annotation { "Feature Type Name" : "Feature", "Feature Type Description" : "" }
export const myFeature = defineFeature(function(context is Context, id is Id, definition is map)
    precondition{}
    {
        {
            var Q0;
            Q0=qCreatedBy(makeId("Top.planeOp"),FACE);
            var sketch = newSketch(context, id + "F0", { "sketchPlane" : qUnion([Q0])});
            skLineSegment(sketch, "E0.bottom", {"start": v(-32.9, 33.13) * mm, "end": v(31.1, 33.13) * mm});
            skLineSegment(sketch, "E0.top", {"start": v(-32.9, -20.87) * mm, "end": v(29.6, -20.87) * mm});
            skLineSegment(sketch, "E0.left", {"start": v(-32.9, 33.13) * mm, "end": v(-32.9, -20.87) * mm});
            skLineSegment(sketch, "E0.right", {"start": v(34.1, 27.13) * mm, "end": v(34.1, -5.87) * mm});
            skLineSegment(sketch, "E1", {"start": v(31.1, 33.13) * mm, "end": v(31.1, 30.13) * mm});
            skLineSegment(sketch, "E2", {"start": v(31.1, -19.37) * mm, "end": v(31.1, -8.87) * mm});
            skLineSegment(sketch, "E3", {"start": v(31.1, 30.13) * mm, "end": v(34.1, 27.13) * mm});
            skLineSegment(sketch, "E4", {"start": v(31.1, -8.87) * mm, "end": v(34.1, -5.87) * mm});
            skLineSegment(sketch, "E5", {"start": v(31.1, 30.13) * mm, "end": v(31.1, -8.87) * mm, "construction": true});
            skCircle(sketch, "E6", {"center": v(31.1, 26.13) * mm, "radius": 1.5 * mm});
            skCircle(sketch, "E7", {"center": v(31.1, -4.87) * mm, "radius": 1.5 * mm});
            skCircle(sketch, "E8", {"center": v(-17.9, -17.87) * mm, "radius": 1.5 * mm});
            skLineSegment(sketch, "E9", {"start": v(-32.9, 6.13) * mm, "end": v(34.1, 6.13) * mm, "construction": true});
            skPoint(sketch, "E9.endSnap0", {"position": v(34.1, 10.63) * mm});
            skCircle(sketch, "E10.MirrorC", {"center": v(-17.9, 30.13) * mm, "radius": 1.5 * mm});
            skLineSegment(sketch, "E11", {"start": v(31.1, -19.37) * mm, "end": v(29.6, -20.87) * mm});
            skPoint(sketch, "E12.orphan", {"position": v(31.1, -20.87) * mm});
            skSolve(sketch);
        }
        {
            var Q0;
            Q0=makeQuery(id+"F0.imprint","IMPRINT",FACE,{"disambiguationData":[TD([[makeQuery(id+"F0.imprint","IMPRINT",EDGE,{"derivedFrom":sQuery(id+"F0.wireOp",EDGE,"E0.bottom")}),-1.0]])]});
            extrude(context, id + "F1", {"entities" : qUnion([Q0]), "depth" : 1.5 * mm});
        }
        {
            var Q0;
            Q0=makeQuery(id+"F1.opExtrude","CAP_FACE",FACE,{"disambiguationData":[OSD([sQuery(id+"F0.wireOp",EDGE,"E0.bottom"),sQuery(id+"F0.wireOp",EDGE,"E0.top"),sQuery(id+"F0.wireOp",EDGE,"E0.left"),sQuery(id+"F0.wireOp",EDGE,"E0.right"),sQuery(id+"F0.wireOp",EDGE,"E1"),sQuery(id+"F0.wireOp",EDGE,"E2"),sQuery(id+"F0.wireOp",EDGE,"E3"),sQuery(id+"F0.wireOp",EDGE,"E4"),sQuery(id+"F0.wireOp",EDGE,"E6"),sQuery(id+"F0.wireOp",EDGE,"E7"),sQuery(id+"F0.wireOp",EDGE,"E8"),sQuery(id+"F0.wireOp",EDGE,"E10.MirrorC"),sQuery(id+"F0.wireOp",EDGE,"E11")])],"isStart":true});
            var sketch = newSketch(context, id + "F2", { "sketchPlane" : qUnion([Q0])});
            skLineSegment(sketch, "E13.bottom", {"start": v(14.85, -30.13) * mm, "end": v(29.85, -30.13) * mm});
            skLineSegment(sketch, "E13.top", {"start": v(14.85, -32.13) * mm, "end": v(29.85, -32.13) * mm});
            skLineSegment(sketch, "E13.left", {"start": v(14.85, -30.13) * mm, "end": v(14.85, -32.13) * mm});
            skLineSegment(sketch, "E13.right", {"start": v(29.85, -30.13) * mm, "end": v(29.85, -32.13) * mm});
            skLineSegment(sketch, "E14.bottom", {"start": v(12.85, -32.13) * mm, "end": v(-2.15, -32.13) * mm});
            skLineSegment(sketch, "E14.top", {"start": v(12.85, -30.13) * mm, "end": v(-2.15, -30.13) * mm});
            skLineSegment(sketch, "E14.left", {"start": v(12.85, -32.13) * mm, "end": v(12.85, -30.13) * mm});
            skLineSegment(sketch, "E14.right", {"start": v(-2.15, -32.13) * mm, "end": v(-2.15, -30.13) * mm});
            skCircle(sketch, "E15", {"center": v(-5.15, -28.13) * mm, "radius": 3 * mm});
            skCircle(sketch, "E16", {"center": v(-11.15, -28.13) * mm, "radius": 3 * mm});
            skSolve(sketch);
        }
        {
            var Q0;
            Q0=makeQuery(id+"F2.imprint","IMPRINT",FACE,{"disambiguationData":[TD([[makeQuery(id+"F2.imprint","IMPRINT",EDGE,{"derivedFrom":sQuery(id+"F2.wireOp",EDGE,"E14.bottom")}),-1.0]])]});
            var Q1;
            Q1=makeQuery(id+"F2.imprint","IMPRINT",FACE,{"disambiguationData":[TD([[makeQuery(id+"F2.imprint","IMPRINT",EDGE,{"derivedFrom":sQuery(id+"F2.wireOp",EDGE,"E13.bottom")}),-1.0]])]});
            extrude(context, id + "F3", {"entities" : qUnion([Q0, Q1]), "depth" : 9 * mm});
        }
        {
            var Q0;
            Q0=makeQuery(id+"F2.imprint","IMPRINT",FACE,{"disambiguationData":[TD([[makeQuery(id+"F2.imprint","IMPRINT",EDGE,{"derivedFrom":sQuery(id+"F2.wireOp",EDGE,"E16")}),1.0]])]});
            var Q1;
            Q1=makeQuery(id+"F2.imprint","IMPRINT",FACE,{"disambiguationData":[TD([[makeQuery(id+"F2.imprint","IMPRINT",EDGE,{"derivedFrom":sQuery(id+"F2.wireOp",EDGE,"E15")}),1.0]])]});
            extrude(context, id + "F4", {"entities" : qUnion([Q0, Q1]), "depth" : 7.5 * mm});
        }
        {
            var Q0;
            Q0=makeQuery(id+"F3.opExtrude","CAP_FACE",FACE,{"disambiguationData":[OSD([sQuery(id+"F2.wireOp",EDGE,"E13.bottom"),sQuery(id+"F2.wireOp",EDGE,"E13.top"),sQuery(id+"F2.wireOp",EDGE,"E13.left"),sQuery(id+"F2.wireOp",EDGE,"E13.right")])],"isStart":false});
            var sketch = newSketch(context, id + "F5", { "sketchPlane" : qUnion([Q0])});
            skLineSegment(sketch, "E17.bottom", {"start": v(15.86, -30.63) * mm, "end": v(17.06, -30.63) * mm});
            skLineSegment(sketch, "E17.top", {"start": v(15.86, -31.83) * mm, "end": v(17.06, -31.83) * mm});
            skLineSegment(sketch, "E17.left", {"start": v(15.86, -30.63) * mm, "end": v(15.86, -31.83) * mm});
            skLineSegment(sketch, "E17.right", {"start": v(17.06, -30.63) * mm, "end": v(17.06, -31.83) * mm});
            skLineSegment(sketch, "E18.bottom", {"start": v(18.34, -30.63) * mm, "end": v(19.54, -30.63) * mm});
            skLineSegment(sketch, "E18.top", {"start": v(18.34, -31.83) * mm, "end": v(19.54, -31.83) * mm});
            skLineSegment(sketch, "E18.left", {"start": v(18.34, -30.63) * mm, "end": v(18.34, -31.83) * mm});
            skLineSegment(sketch, "E18.right", {"start": v(19.54, -30.63) * mm, "end": v(19.54, -31.83) * mm});
            skLineSegment(sketch, "E19.bottom", {"start": v(20.62, -30.63) * mm, "end": v(21.82, -30.63) * mm});
            skLineSegment(sketch, "E19.top", {"start": v(20.62, -31.83) * mm, "end": v(21.82, -31.83) * mm});
            skLineSegment(sketch, "E19.left", {"start": v(20.62, -30.63) * mm, "end": v(20.62, -31.83) * mm});
            skLineSegment(sketch, "E19.right", {"start": v(21.82, -30.63) * mm, "end": v(21.82, -31.83) * mm});
            skLineSegment(sketch, "E20.bottom", {"start": v(23.09, -30.63) * mm, "end": v(24.29, -30.63) * mm});
            skLineSegment(sketch, "E20.top", {"start": v(23.09, -31.83) * mm, "end": v(24.29, -31.83) * mm});
            skLineSegment(sketch, "E20.left", {"start": v(23.09, -30.63) * mm, "end": v(23.09, -31.83) * mm});
            skLineSegment(sketch, "E20.right", {"start": v(24.29, -30.63) * mm, "end": v(24.29, -31.83) * mm});
            skLineSegment(sketch, "E21.bottom", {"start": v(25.37, -30.63) * mm, "end": v(26.57, -30.63) * mm});
            skLineSegment(sketch, "E21.top", {"start": v(25.37, -31.83) * mm, "end": v(26.57, -31.83) * mm});
            skLineSegment(sketch, "E21.left", {"start": v(25.37, -30.63) * mm, "end": v(25.37, -31.83) * mm});
            skLineSegment(sketch, "E21.right", {"start": v(26.57, -30.63) * mm, "end": v(26.57, -31.83) * mm});
            skLineSegment(sketch, "E22.bottom", {"start": v(27.65, -30.63) * mm, "end": v(28.85, -30.63) * mm});
            skLineSegment(sketch, "E22.top", {"start": v(27.65, -31.83) * mm, "end": v(28.85, -31.83) * mm});
            skLineSegment(sketch, "E22.left", {"start": v(27.65, -30.63) * mm, "end": v(27.65, -31.83) * mm});
            skLineSegment(sketch, "E22.right", {"start": v(28.85, -30.63) * mm, "end": v(28.85, -31.83) * mm});
            skLineSegment(sketch, "E23", {"start": v(13.85, -18.98) * mm, "end": v(13.85, -37.75) * mm, "construction": true});
            skLineSegment(sketch, "E24.MirrorCS", {"start": v(11.83, -30.63) * mm, "end": v(10.63, -30.63) * mm});
            skLineSegment(sketch, "E25.MirrorCS", {"start": v(11.83, -30.63) * mm, "end": v(11.83, -31.83) * mm});
            skLineSegment(sketch, "E26.MirrorCS", {"start": v(11.83, -31.83) * mm, "end": v(10.63, -31.83) * mm});
            skLineSegment(sketch, "E27.MirrorCS", {"start": v(10.63, -30.63) * mm, "end": v(10.63, -31.83) * mm});
            skLineSegment(sketch, "E28.MirrorCS", {"start": v(9.36, -30.63) * mm, "end": v(9.36, -31.83) * mm});
            skLineSegment(sketch, "E29.MirrorCS", {"start": v(9.36, -30.63) * mm, "end": v(8.16, -30.63) * mm});
            skLineSegment(sketch, "E30.MirrorCS", {"start": v(8.16, -30.63) * mm, "end": v(8.16, -31.83) * mm});
            skLineSegment(sketch, "E31.MirrorCS", {"start": v(9.36, -31.83) * mm, "end": v(8.16, -31.83) * mm});
            skLineSegment(sketch, "E32.MirrorCS", {"start": v(7.07, -30.63) * mm, "end": v(7.07, -31.83) * mm});
            skLineSegment(sketch, "E33.MirrorCS", {"start": v(7.07, -30.63) * mm, "end": v(5.87, -30.63) * mm});
            skLineSegment(sketch, "E34.MirrorCS", {"start": v(5.87, -30.63) * mm, "end": v(5.87, -31.83) * mm});
            skLineSegment(sketch, "E35.MirrorCS", {"start": v(7.07, -31.83) * mm, "end": v(5.87, -31.83) * mm});
            skLineSegment(sketch, "E36.MirrorCS", {"start": v(4.6, -30.63) * mm, "end": v(4.6, -31.83) * mm});
            skLineSegment(sketch, "E37.MirrorCS", {"start": v(4.6, -30.63) * mm, "end": v(3.4, -30.63) * mm});
            skLineSegment(sketch, "E38.MirrorCS", {"start": v(3.4, -30.63) * mm, "end": v(3.4, -31.83) * mm});
            skLineSegment(sketch, "E39.MirrorCS", {"start": v(4.6, -31.83) * mm, "end": v(3.4, -31.83) * mm});
            skLineSegment(sketch, "E40.MirrorCS", {"start": v(2.32, -30.63) * mm, "end": v(2.32, -31.83) * mm});
            skLineSegment(sketch, "E41.MirrorCS", {"start": v(2.32, -30.63) * mm, "end": v(1.12, -30.63) * mm});
            skLineSegment(sketch, "E42.MirrorCS", {"start": v(1.12, -30.63) * mm, "end": v(1.12, -31.83) * mm});
            skLineSegment(sketch, "E43.MirrorCS", {"start": v(2.32, -31.83) * mm, "end": v(1.12, -31.83) * mm});
            skLineSegment(sketch, "E44.MirrorCS", {"start": v(0.04, -30.63) * mm, "end": v(0.04, -31.83) * mm});
            skLineSegment(sketch, "E45.MirrorCS", {"start": v(0.04, -30.63) * mm, "end": v(-1.16, -30.63) * mm});
            skLineSegment(sketch, "E46.MirrorCS", {"start": v(-1.16, -30.63) * mm, "end": v(-1.16, -31.83) * mm});
            skLineSegment(sketch, "E47.MirrorCS", {"start": v(0.04, -31.83) * mm, "end": v(-1.16, -31.83) * mm});
            skSolve(sketch);
        }
        {
            var Q0;
            Q0=makeQuery(id+"F5.imprint","IMPRINT",FACE,{"disambiguationData":[TD([[makeQuery(id+"F5.imprint","IMPRINT",EDGE,{"derivedFrom":sQuery(id+"F5.wireOp",EDGE,"E17.bottom")}),-1.0]])]});
            var Q1;
            Q1=makeQuery(id+"F5.imprint","IMPRINT",FACE,{"disambiguationData":[TD([[makeQuery(id+"F5.imprint","IMPRINT",EDGE,{"derivedFrom":sQuery(id+"F5.wireOp",EDGE,"E18.bottom")}),-1.0]])]});
            var Q2;
            Q2=makeQuery(id+"F5.imprint","IMPRINT",FACE,{"disambiguationData":[TD([[makeQuery(id+"F5.imprint","IMPRINT",EDGE,{"derivedFrom":sQuery(id+"F5.wireOp",EDGE,"E19.bottom")}),-1.0]])]});
            var Q3;
            Q3=makeQuery(id+"F5.imprint","IMPRINT",FACE,{"disambiguationData":[TD([[makeQuery(id+"F5.imprint","IMPRINT",EDGE,{"derivedFrom":sQuery(id+"F5.wireOp",EDGE,"E20.bottom")}),-1.0]])]});
            var Q4;
            Q4=makeQuery(id+"F5.imprint","IMPRINT",FACE,{"disambiguationData":[TD([[makeQuery(id+"F5.imprint","IMPRINT",EDGE,{"derivedFrom":sQuery(id+"F5.wireOp",EDGE,"E21.bottom")}),-1.0]])]});
            var Q5;
            Q5=makeQuery(id+"F5.imprint","IMPRINT",FACE,{"disambiguationData":[TD([[makeQuery(id+"F5.imprint","IMPRINT",EDGE,{"derivedFrom":sQuery(id+"F5.wireOp",EDGE,"E22.bottom")}),-1.0]])]});
            extrude(context, id + "F6", {"entities" : qUnion([Q0, Q1, Q2, Q3, Q4, Q5]), "operationType" : NewBodyOperationType.REMOVE, "oppositeDirection" : true, "depth" : 3 * mm});
        }
        {
            var Q0;
            Q0=makeQuery(id+"F5.imprint","IMPRINT",FACE,{"disambiguationData":[TD([[makeQuery(id+"F5.imprint","IMPRINT",EDGE,{"derivedFrom":sQuery(id+"F5.wireOp",EDGE,"E44.MirrorCS")}),-1.0]])]});
            var Q1;
            Q1=makeQuery(id+"F5.imprint","IMPRINT",FACE,{"disambiguationData":[TD([[makeQuery(id+"F5.imprint","IMPRINT",EDGE,{"derivedFrom":sQuery(id+"F5.wireOp",EDGE,"E40.MirrorCS")}),-1.0]])]});
            var Q2;
            Q2=makeQuery(id+"F5.imprint","IMPRINT",FACE,{"disambiguationData":[TD([[makeQuery(id+"F5.imprint","IMPRINT",EDGE,{"derivedFrom":sQuery(id+"F5.wireOp",EDGE,"E36.MirrorCS")}),-1.0]])]});
            var Q3;
            Q3=makeQuery(id+"F5.imprint","IMPRINT",FACE,{"disambiguationData":[TD([[makeQuery(id+"F5.imprint","IMPRINT",EDGE,{"derivedFrom":sQuery(id+"F5.wireOp",EDGE,"E32.MirrorCS")}),-1.0]])]});
            var Q4;
            Q4=makeQuery(id+"F5.imprint","IMPRINT",FACE,{"disambiguationData":[TD([[makeQuery(id+"F5.imprint","IMPRINT",EDGE,{"derivedFrom":sQuery(id+"F5.wireOp",EDGE,"E28.MirrorCS")}),-1.0]])]});
            var Q5;
            Q5=makeQuery(id+"F5.imprint","IMPRINT",FACE,{"disambiguationData":[TD([[makeQuery(id+"F5.imprint","IMPRINT",EDGE,{"derivedFrom":sQuery(id+"F5.wireOp",EDGE,"E24.MirrorCS")}),1.0]])]});
            extrude(context, id + "F7", {"entities" : qUnion([Q0, Q1, Q2, Q3, Q4, Q5]), "operationType" : NewBodyOperationType.REMOVE, "oppositeDirection" : true, "depth" : 3 * mm});
        }
        {
            var Q0;
            Q0=makeQuery(id+"F1.opExtrude","CAP_FACE",FACE,{"disambiguationData":[OSD([sQuery(id+"F0.wireOp",EDGE,"E0.bottom"),sQuery(id+"F0.wireOp",EDGE,"E0.top"),sQuery(id+"F0.wireOp",EDGE,"E0.left"),sQuery(id+"F0.wireOp",EDGE,"E0.right"),sQuery(id+"F0.wireOp",EDGE,"E1"),sQuery(id+"F0.wireOp",EDGE,"E2"),sQuery(id+"F0.wireOp",EDGE,"E3"),sQuery(id+"F0.wireOp",EDGE,"E4"),sQuery(id+"F0.wireOp",EDGE,"E6"),sQuery(id+"F0.wireOp",EDGE,"E7"),sQuery(id+"F0.wireOp",EDGE,"E8"),sQuery(id+"F0.wireOp",EDGE,"E10.MirrorC"),sQuery(id+"F0.wireOp",EDGE,"E11")])],"isStart":false});
            var sketch = newSketch(context, id + "F8", { "sketchPlane" : qUnion([Q0])});
            skText(sketch, "E48", { "text": "Mallory Brodnik\nShreya Vinjamuri", "fontName": "AllertaStencil-Regular.ttf"});
            const initialGuessF8  = {"E48": [-0.0289, 0.01572, 1, 0, 0.00513]};
            skSetInitialGuess(sketch, initialGuessF8);
            skSolve(sketch);
        }
        {
            var Q0;
            Q0=qSketchRegion(id+"F8",true);
            extrude(context, id + "F9", {"entities" : qUnion([Q0]), "operationType" : NewBodyOperationType.ADD, "depth" : 0.1 * mm});
        }
        {
            var Q0;
            Q0=makeQuery(id+"F2.imprint","IMPRINT",FACE,{"disambiguationData":[TD([[makeQuery(id+"F2.imprint","IMPRINT",EDGE,{"derivedFrom":sQuery(id+"F2.wireOp",EDGE,"E13.bottom")}),1.0]])]});
            var sketch = newSketch(context, id + "F10", { "sketchPlane" : qUnion([Q0])});
            skLineSegment(sketch, "E49.bottom", {"start": v(-18.88, 12.34) * mm, "end": v(-8.88, 12.34) * mm});
            skLineSegment(sketch, "E49.top", {"start": v(-18.88, 7.34) * mm, "end": v(-8.88, 7.34) * mm});
            skLineSegment(sketch, "E49.left", {"start": v(-18.88, 12.34) * mm, "end": v(-18.88, 7.34) * mm});
            skLineSegment(sketch, "E49.right", {"start": v(-8.88, 12.34) * mm, "end": v(-8.88, 7.34) * mm});
            skSolve(sketch);
        }
        {
            var Q0;
            Q0=makeQuery(id+"F2.imprint","IMPRINT",FACE,{"disambiguationData":[TD([[makeQuery(id+"F2.imprint","IMPRINT",EDGE,{"derivedFrom":sQuery(id+"F2.wireOp",EDGE,"E13.bottom")}),1.0]])]});
            var sketch = newSketch(context, id + "F11", { "sketchPlane" : qUnion([Q0])});
            skLineSegment(sketch, "E50.bottom", {"start": v(3, -2.2) * mm, "end": v(6, -2.2) * mm});
            skLineSegment(sketch, "E50.top", {"start": v(3, -7.2) * mm, "end": v(6, -7.2) * mm});
            skLineSegment(sketch, "E50.left", {"start": v(3, -2.2) * mm, "end": v(3, -7.2) * mm});
            skLineSegment(sketch, "E50.right", {"start": v(6, -2.2) * mm, "end": v(6, -7.2) * mm});
            skSolve(sketch);
        }
        {
            var Q0;
            Q0=makeQuery(id+"F2.imprint","IMPRINT",FACE,{"disambiguationData":[TD([[makeQuery(id+"F2.imprint","IMPRINT",EDGE,{"derivedFrom":sQuery(id+"F2.wireOp",EDGE,"E13.bottom")}),1.0]])]});
            var sketch = newSketch(context, id + "F12", { "sketchPlane" : qUnion([Q0])});
            skLineSegment(sketch, "E51.bottom", {"start": v(-17.42, -21.25) * mm, "end": v(-13.42, -21.25) * mm});
            skLineSegment(sketch, "E51.top", {"start": v(-17.42, -23.75) * mm, "end": v(-13.42, -23.75) * mm});
            skLineSegment(sketch, "E51.left", {"start": v(-17.42, -21.25) * mm, "end": v(-17.42, -23.75) * mm});
            skLineSegment(sketch, "E51.right", {"start": v(-13.42, -21.25) * mm, "end": v(-13.42, -23.75) * mm});
            skSolve(sketch);
        }
        {
            var Q0;
            Q0=makeQuery(id+"F10.imprint","IMPRINT",FACE,{"disambiguationData":[TD([[makeQuery(id+"F10.imprint","IMPRINT",EDGE,{"derivedFrom":sQuery(id+"F10.wireOp",EDGE,"E49.bottom")}),1.0]])]});
            var sketch = newSketch(context, id + "F13", { "sketchPlane" : qUnion([Q0])});
            skLineSegment(sketch, "E52.bottom", {"start": v(-5.87, -13.19) * mm, "end": v(29.13, -13.19) * mm});
            skLineSegment(sketch, "E52.top", {"start": v(-5.87, -22.19) * mm, "end": v(29.13, -22.19) * mm});
            skLineSegment(sketch, "E52.left", {"start": v(-5.87, -13.19) * mm, "end": v(-5.87, -22.19) * mm});
            skLineSegment(sketch, "E52.right", {"start": v(29.13, -13.19) * mm, "end": v(29.13, -22.19) * mm});
            skSolve(sketch);
        }
        {
            var Q0;
            Q0=makeQuery(id+"F10.imprint","IMPRINT",FACE,{"disambiguationData":[TD([[makeQuery(id+"F10.imprint","IMPRINT",EDGE,{"derivedFrom":sQuery(id+"F10.wireOp",EDGE,"E49.bottom")}),1.0]])]});
            var sketch = newSketch(context, id + "F14", { "sketchPlane" : qUnion([Q0])});
            skLineSegment(sketch, "E53.bottom", {"start": v(30.1, 17.37) * mm, "end": v(9.1, 17.37) * mm});
            skLineSegment(sketch, "E53.top", {"start": v(30.1, 19.87) * mm, "end": v(9.1, 19.87) * mm});
            skLineSegment(sketch, "E53.left", {"start": v(30.1, 17.37) * mm, "end": v(30.1, 19.87) * mm});
            skLineSegment(sketch, "E53.right", {"start": v(9.1, 17.37) * mm, "end": v(9.1, 19.87) * mm});
            skLineSegment(sketch, "E54.bottom", {"start": v(-12.9, 19.87) * mm, "end": v(8.1, 19.87) * mm});
            skLineSegment(sketch, "E54.top", {"start": v(-12.9, 17.37) * mm, "end": v(8.1, 17.37) * mm});
            skLineSegment(sketch, "E54.left", {"start": v(-12.9, 19.87) * mm, "end": v(-12.9, 17.37) * mm});
            skLineSegment(sketch, "E54.right", {"start": v(8.1, 19.87) * mm, "end": v(8.1, 17.37) * mm});
            skSolve(sketch);
        }
        {
            var Q0;
            Q0=qSketchRegion(id+"F14",true);
            extrude(context, id + "F15", {"entities" : qUnion([Q0]), "operationType" : NewBodyOperationType.ADD, "depth" : 8 * mm});
        }
        {
            var Q0;
            Q0=makeQuery(id+"F15.opExtrude","CAP_FACE",FACE,{"disambiguationData":[OSD([sQuery(id+"F14.wireOp",EDGE,"E54.bottom"),sQuery(id+"F14.wireOp",EDGE,"E54.top"),sQuery(id+"F14.wireOp",EDGE,"E54.left"),sQuery(id+"F14.wireOp",EDGE,"E54.right")])],"isStart":false});
            var sketch = newSketch(context, id + "F16", { "sketchPlane" : qUnion([Q0])});
            skLineSegment(sketch, "E55.bottom", {"start": v(-12.26, 19.37) * mm, "end": v(-10.76, 19.37) * mm});
            skLineSegment(sketch, "E55.top", {"start": v(-12.26, 17.87) * mm, "end": v(-10.76, 17.87) * mm});
            skLineSegment(sketch, "E55.left", {"start": v(-12.26, 19.37) * mm, "end": v(-12.26, 17.87) * mm});
            skLineSegment(sketch, "E55.right", {"start": v(-10.76, 19.37) * mm, "end": v(-10.76, 17.87) * mm});
            skLineSegment(sketch, "E56.bottom", {"start": v(-9.72, 19.37) * mm, "end": v(-8.22, 19.37) * mm});
            skLineSegment(sketch, "E56.top", {"start": v(-9.72, 17.87) * mm, "end": v(-8.22, 17.87) * mm});
            skLineSegment(sketch, "E56.left", {"start": v(-9.72, 19.37) * mm, "end": v(-9.72, 17.87) * mm});
            skLineSegment(sketch, "E56.right", {"start": v(-8.22, 19.37) * mm, "end": v(-8.22, 17.87) * mm});
            skLineSegment(sketch, "E57.bottom", {"start": v(-7.17, 19.37) * mm, "end": v(-5.67, 19.37) * mm});
            skLineSegment(sketch, "E57.top", {"start": v(-7.17, 17.87) * mm, "end": v(-5.67, 17.87) * mm});
            skLineSegment(sketch, "E57.left", {"start": v(-7.17, 19.37) * mm, "end": v(-7.17, 17.87) * mm});
            skLineSegment(sketch, "E57.right", {"start": v(-5.67, 19.37) * mm, "end": v(-5.67, 17.87) * mm});
            skLineSegment(sketch, "E58.bottom", {"start": v(-4.8, 19.37) * mm, "end": v(-3.3, 19.37) * mm});
            skLineSegment(sketch, "E58.top", {"start": v(-4.8, 17.87) * mm, "end": v(-3.3, 17.87) * mm});
            skLineSegment(sketch, "E58.left", {"start": v(-4.8, 19.37) * mm, "end": v(-4.8, 17.87) * mm});
            skLineSegment(sketch, "E58.right", {"start": v(-3.3, 19.37) * mm, "end": v(-3.3, 17.87) * mm});
            skLineSegment(sketch, "E59.bottom", {"start": v(-2.2, 19.37) * mm, "end": v(-0.7, 19.37) * mm});
            skLineSegment(sketch, "E59.top", {"start": v(-2.2, 17.87) * mm, "end": v(-0.7, 17.87) * mm});
            skLineSegment(sketch, "E59.left", {"start": v(-2.2, 19.37) * mm, "end": v(-2.2, 17.87) * mm});
            skLineSegment(sketch, "E59.right", {"start": v(-0.7, 19.37) * mm, "end": v(-0.7, 17.87) * mm});
            skLineSegment(sketch, "E60.bottom", {"start": v(0.3, 19.37) * mm, "end": v(1.8, 19.37) * mm});
            skLineSegment(sketch, "E60.top", {"start": v(0.3, 17.87) * mm, "end": v(1.8, 17.87) * mm});
            skLineSegment(sketch, "E60.left", {"start": v(0.3, 19.37) * mm, "end": v(0.3, 17.87) * mm});
            skLineSegment(sketch, "E60.right", {"start": v(1.8, 19.37) * mm, "end": v(1.8, 17.87) * mm});
            skLineSegment(sketch, "E61.bottom", {"start": v(2.9, 19.37) * mm, "end": v(4.4, 19.37) * mm});
            skLineSegment(sketch, "E61.top", {"start": v(2.9, 17.87) * mm, "end": v(4.4, 17.87) * mm});
            skLineSegment(sketch, "E61.left", {"start": v(2.9, 19.37) * mm, "end": v(2.9, 17.87) * mm});
            skLineSegment(sketch, "E61.right", {"start": v(4.4, 19.37) * mm, "end": v(4.4, 17.87) * mm});
            skLineSegment(sketch, "E62.bottom", {"start": v(5.56, 19.37) * mm, "end": v(7.06, 19.37) * mm});
            skLineSegment(sketch, "E62.top", {"start": v(5.56, 17.87) * mm, "end": v(7.06, 17.87) * mm});
            skLineSegment(sketch, "E62.left", {"start": v(5.56, 19.37) * mm, "end": v(5.56, 17.87) * mm});
            skLineSegment(sketch, "E62.right", {"start": v(7.06, 19.37) * mm, "end": v(7.06, 17.87) * mm});
            skLineSegment(sketch, "E63", {"start": v(8.6, 21.66) * mm, "end": v(8.6, 8.99) * mm, "construction": true});
            skLineSegment(sketch, "E64.MirrorCS", {"start": v(10.13, 19.37) * mm, "end": v(10.13, 17.87) * mm});
            skLineSegment(sketch, "E65.MirrorCS", {"start": v(11.63, 17.87) * mm, "end": v(10.13, 17.87) * mm});
            skLineSegment(sketch, "E66.MirrorCS", {"start": v(11.63, 19.37) * mm, "end": v(11.63, 17.87) * mm});
            skLineSegment(sketch, "E67.MirrorCS", {"start": v(11.63, 19.37) * mm, "end": v(10.13, 19.37) * mm});
            skLineSegment(sketch, "E68.MirrorCS", {"start": v(14.3, 19.37) * mm, "end": v(12.8, 19.37) * mm});
            skLineSegment(sketch, "E69.MirrorCS", {"start": v(14.3, 19.37) * mm, "end": v(14.3, 17.87) * mm});
            skLineSegment(sketch, "E70.MirrorCS", {"start": v(14.3, 17.87) * mm, "end": v(12.8, 17.87) * mm});
            skLineSegment(sketch, "E71.MirrorCS", {"start": v(12.8, 19.37) * mm, "end": v(12.8, 17.87) * mm});
            skLineSegment(sketch, "E72.MirrorCS", {"start": v(16.9, 17.87) * mm, "end": v(15.4, 17.87) * mm});
            skLineSegment(sketch, "E73.MirrorCS", {"start": v(16.9, 19.37) * mm, "end": v(16.9, 17.87) * mm});
            skLineSegment(sketch, "E74.MirrorCS", {"start": v(16.9, 19.37) * mm, "end": v(15.4, 19.37) * mm});
            skLineSegment(sketch, "E75.MirrorCS", {"start": v(15.4, 19.37) * mm, "end": v(15.4, 17.87) * mm});
            skLineSegment(sketch, "E76.MirrorCS", {"start": v(17.88, 19.37) * mm, "end": v(17.88, 17.87) * mm});
            skLineSegment(sketch, "E77.MirrorCS", {"start": v(19.38, 19.37) * mm, "end": v(17.88, 19.37) * mm});
            skLineSegment(sketch, "E78.MirrorCS", {"start": v(19.38, 19.37) * mm, "end": v(19.38, 17.87) * mm});
            skLineSegment(sketch, "E79.MirrorCS", {"start": v(19.38, 17.87) * mm, "end": v(17.88, 17.87) * mm});
            skLineSegment(sketch, "E80.MirrorCS", {"start": v(20.49, 19.37) * mm, "end": v(20.49, 17.87) * mm});
            skLineSegment(sketch, "E81.MirrorCS", {"start": v(21.99, 19.37) * mm, "end": v(20.49, 19.37) * mm});
            skLineSegment(sketch, "E82.MirrorCS", {"start": v(21.99, 19.37) * mm, "end": v(21.99, 17.87) * mm});
            skLineSegment(sketch, "E83.MirrorCS", {"start": v(21.99, 17.87) * mm, "end": v(20.49, 17.87) * mm});
            skLineSegment(sketch, "E84.MirrorCS", {"start": v(22.86, 19.37) * mm, "end": v(22.86, 17.87) * mm});
            skLineSegment(sketch, "E85.MirrorCS", {"start": v(24.36, 19.37) * mm, "end": v(22.86, 19.37) * mm});
            skLineSegment(sketch, "E86.MirrorCS", {"start": v(24.36, 19.37) * mm, "end": v(24.36, 17.87) * mm});
            skLineSegment(sketch, "E87.MirrorCS", {"start": v(24.36, 17.87) * mm, "end": v(22.86, 17.87) * mm});
            skLineSegment(sketch, "E88.MirrorCS", {"start": v(26.9, 17.87) * mm, "end": v(25.4, 17.87) * mm});
            skLineSegment(sketch, "E89.MirrorCS", {"start": v(26.9, 19.37) * mm, "end": v(26.9, 17.87) * mm});
            skLineSegment(sketch, "E90.MirrorCS", {"start": v(26.9, 19.37) * mm, "end": v(25.4, 19.37) * mm});
            skLineSegment(sketch, "E91.MirrorCS", {"start": v(25.4, 19.37) * mm, "end": v(25.4, 17.87) * mm});
            skLineSegment(sketch, "E92.MirrorCS", {"start": v(27.95, 19.37) * mm, "end": v(27.95, 17.87) * mm});
            skLineSegment(sketch, "E93.MirrorCS", {"start": v(29.45, 19.37) * mm, "end": v(27.95, 19.37) * mm});
            skLineSegment(sketch, "E94.MirrorCS", {"start": v(29.45, 19.37) * mm, "end": v(29.45, 17.87) * mm});
            skLineSegment(sketch, "E95.MirrorCS", {"start": v(29.45, 17.87) * mm, "end": v(27.95, 17.87) * mm});
            skSolve(sketch);
        }
        {
            var Q0;
            Q0=qSketchRegion(id+"F16",true);
            extrude(context, id + "F17", {"entities" : qUnion([Q0]), "operationType" : NewBodyOperationType.REMOVE, "oppositeDirection" : true, "depth" : 5 * mm});
        }
        {
            var Q0;
            Q0=makeQuery(id+"F10.imprint","IMPRINT",FACE,{"disambiguationData":[TD([[makeQuery(id+"F10.imprint","IMPRINT",EDGE,{"derivedFrom":sQuery(id+"F10.wireOp",EDGE,"E49.bottom")}),-1.0]])]});
            extrude(context, id + "F18", {"entities" : qUnion([Q0]), "depth" : 1.5 * mm});
        }
        {
            var Q0;
            Q0=qSketchRegion(id+"F12",true);
            extrude(context, id + "F19", {"entities" : qUnion([Q0]), "depth" : 3 * mm});
        }
        {
            var Q0;
            Q0=qSketchRegion(id+"F13",true);
            extrude(context, id + "F20", {"entities" : qUnion([Q0]), "depth" : 4.5 * mm});
        }
        {
            var Q0;
            Q0=makeQuery(id+"F11.imprint","IMPRINT",FACE,{"disambiguationData":[TD([[makeQuery(id+"F11.imprint","IMPRINT",EDGE,{"derivedFrom":sQuery(id+"F11.wireOp",EDGE,"E50.bottom")}),-1.0]])]});
            extrude(context, id + "F21", {"entities" : qUnion([Q0]), "depth" : 1 * mm});
        }
        {
            var Q0;
            Q0=makeQuery(id+"F20.opExtrude","CAP_FACE",FACE,{"disambiguationData":[OSD([sQuery(id+"F13.wireOp",EDGE,"E52.bottom"),sQuery(id+"F13.wireOp",EDGE,"E52.top"),sQuery(id+"F13.wireOp",EDGE,"E52.left"),sQuery(id+"F13.wireOp",EDGE,"E52.right")])],"isStart":false});
            var sketch = newSketch(context, id + "F22", { "sketchPlane" : qUnion([Q0])});
            skLineSegment(sketch, "E96.bottom", {"start": v(-5.87, -14.39) * mm, "end": v(29.13, -14.39) * mm});
            skLineSegment(sketch, "E96.top", {"start": v(-5.87, -20.99) * mm, "end": v(29.13, -20.99) * mm});
            skLineSegment(sketch, "E96.left", {"start": v(-5.87, -14.39) * mm, "end": v(-5.87, -20.99) * mm});
            skLineSegment(sketch, "E96.right", {"start": v(29.13, -14.39) * mm, "end": v(29.13, -20.99) * mm});
            skSolve(sketch);
        }
        {
            var Q0;
            Q0=qSketchRegion(id+"F22",true);
            extrude(context, id + "F23", {"entities" : qUnion([Q0]), "depth" : 3.5 * mm});
        }
        {
            var Q0;
            Q0=makeQuery(id+"F2.imprint","IMPRINT",FACE,{"disambiguationData":[TD([[makeQuery(id+"F2.imprint","IMPRINT",EDGE,{"derivedFrom":sQuery(id+"F2.wireOp",EDGE,"E13.bottom")}),1.0]])]});
            var sketch = newSketch(context, id + "F24", { "sketchPlane" : qUnion([Q0])});
            skLineSegment(sketch, "E97.bottom", {"start": v(17.1, -3.13) * mm, "end": v(23.1, -3.13) * mm});
            skLineSegment(sketch, "E97.top", {"start": v(17.1, -9.13) * mm, "end": v(23.1, -9.13) * mm});
            skLineSegment(sketch, "E97.left", {"start": v(17.1, -3.13) * mm, "end": v(17.1, -9.13) * mm});
            skLineSegment(sketch, "E97.right", {"start": v(23.1, -3.13) * mm, "end": v(23.1, -9.13) * mm});
            skSolve(sketch);
        }
        {
            var Q0;
            Q0=qSketchRegion(id+"F24",true);
            extrude(context, id + "F25", {"entities" : qUnion([Q0]), "depth" : 3.7 * mm});
        }
        {
            var Q0;
            Q0=makeQuery(id+"F25.opExtrude","CAP_FACE",FACE,{"disambiguationData":[OSD([sQuery(id+"F24.wireOp",EDGE,"E97.bottom"),sQuery(id+"F24.wireOp",EDGE,"E97.top"),sQuery(id+"F24.wireOp",EDGE,"E97.left"),sQuery(id+"F24.wireOp",EDGE,"E97.right")])],"isStart":false});
            var sketch = newSketch(context, id + "F26", { "sketchPlane" : qUnion([Q0])});
            skCircle(sketch, "E98", {"center": v(20.1, -6.13) * mm, "radius": 1.5 * mm});
            skPoint(sketch, "E98.centerSnap0", {"position": v(23.1, -6.13) * mm});
            skPoint(sketch, "E98.centerSnap1", {"position": v(20.1, -3.13) * mm});
            skCircle(sketch, "E99", {"center": v(17.95, -4.1) * mm, "radius": 0.5 * mm});
            skCircle(sketch, "E100", {"center": v(18.06, -8.09) * mm, "radius": 0.5 * mm});
            skCircle(sketch, "E101", {"center": v(22.15, -4.21) * mm, "radius": 0.5 * mm});
            skCircle(sketch, "E102", {"center": v(22.04, -8.2) * mm, "radius": 0.5 * mm});
            skSolve(sketch);
        }
        {
            var Q0;
            Q0=qSketchRegion(id+"F26",true);
            extrude(context, id + "F27", {"entities" : qUnion([Q0]), "depth" : 0.75 * mm});
        }
        {
            var Q0;
            Q0=makeQuery(id+"F2.imprint","IMPRINT",FACE,{"disambiguationData":[TD([[makeQuery(id+"F2.imprint","IMPRINT",EDGE,{"derivedFrom":sQuery(id+"F2.wireOp",EDGE,"E13.bottom")}),1.0]])]});
            var sketch = newSketch(context, id + "F28", { "sketchPlane" : qUnion([Q0])});
            skLineSegment(sketch, "E103.bottom", {"start": v(-29.9, -13.13) * mm, "end": v(-24.4, -13.13) * mm});
            skLineSegment(sketch, "E103.top", {"start": v(-29.9, -18.63) * mm, "end": v(-24.4, -18.63) * mm});
            skLineSegment(sketch, "E103.left", {"start": v(-29.9, -13.13) * mm, "end": v(-29.9, -18.63) * mm});
            skLineSegment(sketch, "E103.right", {"start": v(-24.4, -13.13) * mm, "end": v(-24.4, -18.63) * mm});
            skSolve(sketch);
        }
        {
            var Q0;
            Q0=qSketchRegion(id+"F28",true);
            extrude(context, id + "F29", {"entities" : qUnion([Q0]), "depth" : 2.5 * mm});
        }
        {
            var Q0;
            Q0=makeQuery(id+"F2.imprint","IMPRINT",FACE,{"disambiguationData":[TD([[makeQuery(id+"F2.imprint","IMPRINT",EDGE,{"derivedFrom":sQuery(id+"F2.wireOp",EDGE,"E13.bottom")}),1.0]])]});
            var sketch = newSketch(context, id + "F30", { "sketchPlane" : qUnion([Q0])});
            skLineSegment(sketch, "E104.bottom", {"start": v(-35.9, 12.87) * mm, "end": v(-27.9, 12.87) * mm});
            skLineSegment(sketch, "E104.top", {"start": v(-35.9, 6.37) * mm, "end": v(-27.9, 6.37) * mm});
            skLineSegment(sketch, "E104.left", {"start": v(-35.9, 12.87) * mm, "end": v(-35.9, 6.37) * mm});
            skLineSegment(sketch, "E104.right", {"start": v(-27.9, 12.87) * mm, "end": v(-27.9, 6.37) * mm});
            skSolve(sketch);
        }
        {
            var Q0;
            Q0=qSketchRegion(id+"F30",true);
            extrude(context, id + "F31", {"entities" : qUnion([Q0]), "depth" : 3.9 * mm});
        }
        {
            var Q0;
            Q0=makeQuery(id+"F31.opExtrude","SWEPT_FACE",FACE,{"disambiguationData":[OSD([sQuery(id+"F30.wireOp",EDGE,"E104.left")])]});
            var sketch = newSketch(context, id + "F32", { "sketchPlane" : qUnion([Q0])});
            skPoint(sketch, "E105.oppositeSnap0", {"position": v(6.37, -1.95) * mm});
            skLineSegment(sketch, "E105.bottom", {"start": v(6.37, 0) * mm, "end": v(7.07, 0) * mm});
            skLineSegment(sketch, "E105.top", {"start": v(6.37, -1.95) * mm, "end": v(7.07, -1.95) * mm});
            skLineSegment(sketch, "E105.left", {"start": v(6.37, 0) * mm, "end": v(6.37, -1.95) * mm});
            skLineSegment(sketch, "E105.right", {"start": v(7.07, 0) * mm, "end": v(7.07, -1.95) * mm});
            skPoint(sketch, "E106.oppositeSnap0", {"position": v(12.87, -1.95) * mm});
            skLineSegment(sketch, "E106.bottom", {"start": v(12.87, 0) * mm, "end": v(12.17, 0) * mm});
            skLineSegment(sketch, "E106.top", {"start": v(12.87, -1.95) * mm, "end": v(12.17, -1.95) * mm});
            skLineSegment(sketch, "E106.left", {"start": v(12.87, 0) * mm, "end": v(12.87, -1.95) * mm});
            skLineSegment(sketch, "E106.right", {"start": v(12.17, 0) * mm, "end": v(12.17, -1.95) * mm});
            skSolve(sketch);
        }
        {
            var Q0;
            Q0=qSketchRegion(id+"F32",true);
            extrude(context, id + "F33", {"entities" : qUnion([Q0]), "operationType" : NewBodyOperationType.REMOVE, "oppositeDirection" : true, "depth" : 3 * mm});
        }
        {
            var Q0;
            Q0=makeQuery(id+"F31.opExtrude","CAP_EDGE",EDGE,{"disambiguationData":[OSD([sQuery(id+"F30.wireOp",EDGE,"E104.top")])],"isStart":false});
            var Q1;
            Q1=makeQuery(id+"F31.opExtrude","CAP_EDGE",EDGE,{"disambiguationData":[OSD([sQuery(id+"F30.wireOp",EDGE,"E104.bottom")])],"isStart":false});
            var Q2;
            Q2=makeQuery(id+"F31.opExtrude","CAP_EDGE",EDGE,{"disambiguationData":[OSD([sQuery(id+"F30.wireOp",EDGE,"E104.right")])],"isStart":false});
            var Q3;
            Q3=makeQuery(id+"F31.opExtrude","SWEPT_EDGE",EDGE,{"disambiguationData":[OSD([sQuery(id+"F30.wireOp",EDGE,"E104.top"),sQuery(id+"F30.wireOp",EDGE,"E104.right")])]});
            var Q4;
            Q4=makeQuery(id+"F33.boolean.opBoolean","COPY",EDGE,{"derivedFrom":makeQuery(id+"F33.opExtrude","SWEPT_EDGE",EDGE,{"disambiguationData":[OSD([sQuery(id+"F30.wireOp",EDGE,"E104.left"),sQuery(id+"F32.wireOp",EDGE,"E105.bottom"),sQuery(id+"F32.wireOp",EDGE,"E105.right")])]})});
            var Q5;
            Q5=makeQuery(id+"F33.boolean.opBoolean","COPY",EDGE,{"derivedFrom":makeQuery(id+"F33.opExtrude","SWEPT_EDGE",EDGE,{"disambiguationData":[OSD([sQuery(id+"F30.wireOp",EDGE,"E104.left"),sQuery(id+"F32.wireOp",EDGE,"E106.bottom"),sQuery(id+"F32.wireOp",EDGE,"E106.right")])]})});
            var Q6;
            Q6=makeQuery(id+"F31.opExtrude","SWEPT_EDGE",EDGE,{"disambiguationData":[OSD([sQuery(id+"F30.wireOp",EDGE,"E104.bottom"),sQuery(id+"F30.wireOp",EDGE,"E104.right")])]});
            fillet(context, id + "F34", {"entities" : qUnion([Q0, Q1, Q2, Q3, Q4, Q5, Q6]), "radius" : 1 * mm, "tangentPropagation" : true, "allowEdgeOverflow" : false});
        }
        {
            var Q0;
            Q0=makeQuery(id+"F33.boolean.opBoolean","COPY",EDGE,{"derivedFrom":makeQuery(id+"F33.opExtrude","SWEPT_EDGE",EDGE,{"disambiguationData":[OSD([sQuery(id+"F32.wireOp",EDGE,"E106.top"),sQuery(id+"F32.wireOp",EDGE,"E106.right")])]})});
            var Q1;
            Q1=makeQuery(id+"F33.boolean.opBoolean","COPY",EDGE,{"derivedFrom":makeQuery(id+"F33.opExtrude","SWEPT_EDGE",EDGE,{"disambiguationData":[OSD([sQuery(id+"F32.wireOp",EDGE,"E105.top"),sQuery(id+"F32.wireOp",EDGE,"E105.right")])]})});
            fillet(context, id + "F35", {"entities" : qUnion([Q0, Q1]), "radius" : 1 * mm, "tangentPropagation" : true, "allowEdgeOverflow" : false});
        }
        {
            var Q0;
            Q0=makeQuery(id+"F35.opFillet","BLEND_EDGE",EDGE,{"blendedFrom":[makeQuery(id+"F33.boolean.opBoolean","COPY",EDGE,{"derivedFrom":makeQuery(id+"F33.opExtrude","SWEPT_EDGE",EDGE,{"disambiguationData":[OSD([sQuery(id+"F32.wireOp",EDGE,"E105.top"),sQuery(id+"F32.wireOp",EDGE,"E105.right")])]})}),makeQuery(id+"F31.opExtrude","SWEPT_FACE",FACE,{"disambiguationData":[OSD([sQuery(id+"F30.wireOp",EDGE,"E104.top")])]})],"blendedInto":[makeQuery(id+"F31.opExtrude","SWEPT_FACE",FACE,{"disambiguationData":[OSD([sQuery(id+"F30.wireOp",EDGE,"E104.top")])]})]});
            var Q1;
            Q1=makeQuery(id+"F35.opFillet","BLEND_EDGE",EDGE,{"blendedFrom":[makeQuery(id+"F33.boolean.opBoolean","COPY",EDGE,{"derivedFrom":makeQuery(id+"F33.opExtrude","SWEPT_EDGE",EDGE,{"disambiguationData":[OSD([sQuery(id+"F32.wireOp",EDGE,"E106.top"),sQuery(id+"F32.wireOp",EDGE,"E106.right")])]})}),makeQuery(id+"F31.opExtrude","SWEPT_FACE",FACE,{"disambiguationData":[OSD([sQuery(id+"F30.wireOp",EDGE,"E104.bottom")])]})],"blendedInto":[makeQuery(id+"F31.opExtrude","SWEPT_FACE",FACE,{"disambiguationData":[OSD([sQuery(id+"F30.wireOp",EDGE,"E104.bottom")])]})]});
            fillet(context, id + "F36", {"entities" : qUnion([Q0, Q1]), "radius" : 1 * mm, "tangentPropagation" : true, "allowEdgeOverflow" : false});
        }
        {
            var Q0;
            Q0=makeQuery(id+"F31.opExtrude","SWEPT_FACE",FACE,{"disambiguationData":[OSD([sQuery(id+"F30.wireOp",EDGE,"E104.left")])]});
            var Q1;
            Q1=makeQuery(id+"F31.opExtrude","SWEPT_BODY",BODY,{"disambiguationData":[OSD([sQuery(id+"F30.wireOp",EDGE,"E104.bottom"),sQuery(id+"F30.wireOp",EDGE,"E104.top"),sQuery(id+"F30.wireOp",EDGE,"E104.left"),sQuery(id+"F30.wireOp",EDGE,"E104.right")])]});
            shell(context, id + "F37", {"entities" : qUnion([Q0]), "parts" : qUnion([Q1]), "thickness" : 0.2 * mm});
        }
    });